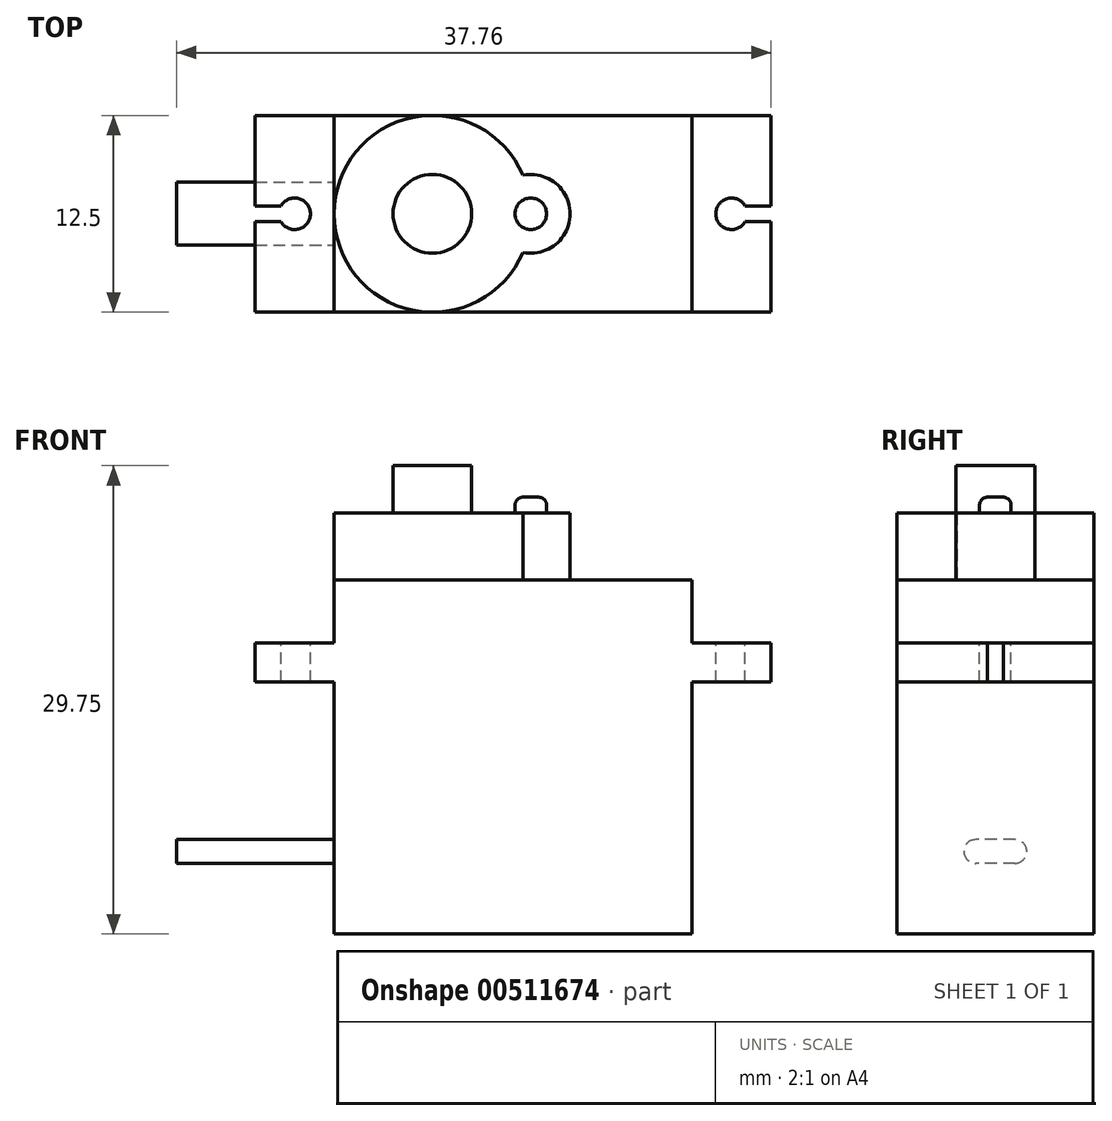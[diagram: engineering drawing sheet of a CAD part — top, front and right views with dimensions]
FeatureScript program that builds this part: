
annotation { "Feature Type Name" : "Feature", "Feature Type Description" : "" }
export const myFeature = defineFeature(function(context is Context, id is Id, definition is map)
    precondition{}
    {
        {
            var Q0;
            Q0=qCreatedBy(makeId("Top.planeOp"),FACE);
            var sketch = newSketch(context, id + "F0", { "sketchPlane" : qUnion([Q0])});
            skLineSegment(sketch, "E0.bottom", {"start": v(11.38, 6.25) * mm, "end": v(-11.37, 6.25) * mm});
            skLineSegment(sketch, "E0.top", {"start": v(11.37, -6.25) * mm, "end": v(-11.38, -6.25) * mm});
            skLineSegment(sketch, "E0.left", {"start": v(11.38, 6.25) * mm, "end": v(11.37, -6.25) * mm});
            skLineSegment(sketch, "E0.right", {"start": v(-11.37, 6.25) * mm, "end": v(-11.38, -6.25) * mm});
            skPoint(sketch, "E0.middle", {"position": v(0, 0) * mm});
            skSolve(sketch);
        }
        {
            var Q0;
            Q0=makeQuery(id+"F0.imprint","IMPRINT",FACE,{"disambiguationData":[TD([[makeQuery(id+"F0.imprint","IMPRINT",EDGE,{"derivedFrom":sQuery(id+"F0.wireOp",EDGE,"E0.bottom")}),1.0]])]});
            extrude(context, id + "F1", {"entities" : qUnion([Q0]), "depth" : 22.5 * mm});
        }
        {
            var Q0;
            Q0=qCreatedBy(makeId("Top.planeOp"),FACE);
            cPlane(context, id + "F2", {"entities" : qUnion([Q0]), "cplaneType" : CPlaneType.OFFSET, "offset" : 16 * mm, "width" : 150 * mm, "height" : 150 * mm});
        }
        {
            var Q0;
            Q0=qCreatedBy(id+"F2.planeOp",FACE);
            var sketch = newSketch(context, id + "F3", { "sketchPlane" : qUnion([Q0])});
            skLineSegment(sketch, "E1.bottom", {"start": v(11.38, 6.25) * mm, "end": v(16.38, 6.25) * mm});
            skLineSegment(sketch, "E1.top", {"start": v(11.38, -6.25) * mm, "end": v(16.38, -6.25) * mm});
            skLineSegment(sketch, "E1.left", {"start": v(11.38, 6.25) * mm, "end": v(11.38, -6.25) * mm});
            skLineSegment(sketch, "E1.right", {"start": v(16.38, 6.25) * mm, "end": v(16.38, -6.25) * mm});
            skLineSegment(sketch, "E2.bottom", {"start": v(-16.38, 6.25) * mm, "end": v(-11.37, 6.25) * mm});
            skLineSegment(sketch, "E2.top", {"start": v(-16.38, -6.25) * mm, "end": v(-11.38, -6.25) * mm});
            skLineSegment(sketch, "E2.left", {"start": v(-16.38, 6.25) * mm, "end": v(-16.38, -6.25) * mm});
            skLineSegment(sketch, "E2.right", {"start": v(-11.37, 6.25) * mm, "end": v(-11.37, -6.25) * mm});
            skSolve(sketch);
        }
        {
            var Q0;
            Q0=makeQuery(id+"F3.imprint","IMPRINT",FACE,{"disambiguationData":[TD([[makeQuery(id+"F3.imprint","IMPRINT",EDGE,{"derivedFrom":sQuery(id+"F3.wireOp",EDGE,"E2.bottom")}),-1.0]])]});
            var Q1;
            Q1=makeQuery(id+"F3.imprint","IMPRINT",FACE,{"disambiguationData":[TD([[makeQuery(id+"F3.imprint","IMPRINT",EDGE,{"derivedFrom":sQuery(id+"F3.wireOp",EDGE,"E1.bottom")}),-1.0]])]});
            extrude(context, id + "F4", {"entities" : qUnion([Q0, Q1]), "operationType" : NewBodyOperationType.ADD, "depth" : 2.5 * mm});
        }
        {
            var Q0;
            Q0=makeQuery(id+"F4.opExtrude","CAP_FACE",FACE,{"disambiguationData":[OSD([sQuery(id+"F3.wireOp",EDGE,"E2.bottom"),sQuery(id+"F3.wireOp",EDGE,"E2.top"),sQuery(id+"F3.wireOp",EDGE,"E2.left"),sQuery(id+"F3.wireOp",EDGE,"E2.right")])],"isStart":false});
            var sketch = newSketch(context, id + "F5", { "sketchPlane" : qUnion([Q0])});
            skArc(sketch, "E3", {"start": v(-14.74, -0.5) * mm, "mid": v(-12.88, 0) * mm, "end": v(-14.74, 0.5) * mm});
            skArc(sketch, "E4", {"start": v(14.74, 0.5) * mm, "mid": v(12.88, 0) * mm, "end": v(14.74, -0.5) * mm});
            skLineSegment(sketch, "E5", {"start": v(-13.88, 0) * mm, "end": v(-16.38, 0) * mm, "construction": true});
            skLineSegment(sketch, "E6", {"start": v(13.88, 0) * mm, "end": v(16.38, 0) * mm, "construction": true});
            skLineSegment(sketch, "E7.0", {"start": v(-14.74, 0.5) * mm, "end": v(-16.38, 0.5) * mm});
            skLineSegment(sketch, "E8.0", {"start": v(-14.74, -0.5) * mm, "end": v(-16.38, -0.5) * mm});
            skLineSegment(sketch, "E9", {"start": v(-16.38, 0.5) * mm, "end": v(-16.38, -0.5) * mm});
            skLineSegment(sketch, "E10.0", {"start": v(14.74, -0.5) * mm, "end": v(16.38, -0.5) * mm});
            skLineSegment(sketch, "E11.0", {"start": v(14.74, 0.5) * mm, "end": v(16.38, 0.5) * mm});
            skLineSegment(sketch, "E12", {"start": v(16.38, 0.5) * mm, "end": v(16.38, -0.5) * mm});
            skSolve(sketch);
        }
        {
            var Q0;
            Q0=makeQuery(id+"F5.imprint","IMPRINT",FACE,{"disambiguationData":[TD([[makeQuery(id+"F5.imprint","IMPRINT",EDGE,{"derivedFrom":sQuery(id+"F5.wireOp",EDGE,"E3")}),1.0]])]});
            var Q1;
            Q1=makeQuery(id+"F5.imprint","IMPRINT",FACE,{"disambiguationData":[TD([[makeQuery(id+"F5.imprint","IMPRINT",EDGE,{"derivedFrom":sQuery(id+"F5.wireOp",EDGE,"E4")}),1.0]])]});
            extrude(context, id + "F6", {"entities" : qUnion([Q0, Q1]), "operationType" : NewBodyOperationType.REMOVE, "endBound" : BoundingType.UP_TO_NEXT, "oppositeDirection" : true, "depth" : 25 * mm});
        }
        {
            var Q0;
            Q0=makeQuery(id+"F1.opExtrude","CAP_FACE",FACE,{"disambiguationData":[OSD([sQuery(id+"F0.wireOp",EDGE,"E0.bottom"),sQuery(id+"F0.wireOp",EDGE,"E0.top"),sQuery(id+"F0.wireOp",EDGE,"E0.left"),sQuery(id+"F0.wireOp",EDGE,"E0.right")])],"isStart":false});
            var sketch = newSketch(context, id + "F7", { "sketchPlane" : qUnion([Q0])});
            skArc(sketch, "E13", {"start": v(0.63, 2.45) * mm, "mid": v(-11.37, 0) * mm, "end": v(0.63, -2.45) * mm});
            skArc(sketch, "E14", {"start": v(0.63, -2.45) * mm, "mid": v(3.63, 0) * mm, "end": v(0.63, 2.45) * mm});
            skSolve(sketch);
        }
        {
            var Q0;
            {var subQ0=sQuery(id+"F7.wireOp",EDGE,"E14");Q0=makeQuery(id+"F7.imprint","IMPRINT",FACE,{"disambiguationData":[TD([[makeQuery(id+"F7.imprint","IMPRINT",EDGE,{"derivedFrom":subQ0}),1.0]])]});}
            extrude(context, id + "F8", {"entities" : qUnion([Q0]), "operationType" : NewBodyOperationType.ADD, "depth" : 4.25 * mm});
        }
        {
            var Q0;
            Q0=makeQuery(id+"F8.opExtrude","CAP_FACE",FACE,{"disambiguationData":[OSD([sQuery(id+"F7.wireOp",EDGE,"E13"),sQuery(id+"F7.wireOp",EDGE,"E14")])],"isStart":false});
            var sketch = newSketch(context, id + "F9", { "sketchPlane" : qUnion([Q0])});
            skCircle(sketch, "E15", {"center": v(1.13, 0) * mm, "radius": 1 * mm});
            skSolve(sketch);
        }
        {
            var Q0;
            Q0=makeQuery(id+"F9.imprint","IMPRINT",FACE,{"disambiguationData":[TD([[makeQuery(id+"F9.imprint","IMPRINT",EDGE,{"derivedFrom":sQuery(id+"F9.wireOp",EDGE,"E15")}),1.0]])]});
            extrude(context, id + "F10", {"entities" : qUnion([Q0]), "operationType" : NewBodyOperationType.ADD, "depth" : 1 * mm});
        }
        {
            var Q0;
            Q0=makeQuery(id+"F8.opExtrude","CAP_FACE",FACE,{"disambiguationData":[OSD([sQuery(id+"F7.wireOp",EDGE,"E13"),sQuery(id+"F7.wireOp",EDGE,"E14")])],"isStart":false});
            var sketch = newSketch(context, id + "F11", { "sketchPlane" : qUnion([Q0])});
            skCircle(sketch, "E16", {"center": v(-5.12, 0) * mm, "radius": 2.5 * mm});
            skSolve(sketch);
        }
        {
            var Q0;
            Q0=makeQuery(id+"F11.imprint","IMPRINT",FACE,{"disambiguationData":[TD([[makeQuery(id+"F11.imprint","IMPRINT",EDGE,{"derivedFrom":sQuery(id+"F11.wireOp",EDGE,"E16")}),1.0]])]});
            extrude(context, id + "F12", {"entities" : qUnion([Q0]), "operationType" : NewBodyOperationType.ADD, "depth" : 3 * mm});
        }
        {
            var Q0;
            {var subQ0=sQuery(id+"F0.wireOp",EDGE,"E0.top");var subQ2=sQuery(id+"F0.wireOp",EDGE,"E0.right");var subQ3=sQuery(id+"F0.wireOp",EDGE,"E0.bottom");Q0=makeQuery(id+"F4.boolean.opBoolean","SPLIT",FACE,{"disambiguationData":[TD([makeQuery(id+"F1.opExtrude","CAP_FACE",FACE,{"disambiguationData":[OSD([subQ3,subQ0,sQuery(id+"F0.wireOp",EDGE,"E0.left"),subQ2])],"isStart":true})])],"derivedFrom":makeQuery(id+"F1.opExtrude","SWEPT_FACE",FACE,{"disambiguationData":[OSD([subQ2])]})});}
            var sketch = newSketch(context, id + "F13", { "sketchPlane" : qUnion([Q0])});
            skLineSegment(sketch, "E17.bottom", {"start": v(-1.25, 6) * mm, "end": v(1.25, 6) * mm});
            skLineSegment(sketch, "E17.top", {"start": v(-1.25, 4.5) * mm, "end": v(1.25, 4.5) * mm});
            skLineSegment(sketch, "E17.left", {"start": v(-2, 5.25) * mm, "end": v(-2, 5.25) * mm});
            skLineSegment(sketch, "E17.right", {"start": v(2, 5.25) * mm, "end": v(2, 5.25) * mm});
            skPoint(sketch, "E18.visualSharp", {"position": v(-2, 6) * mm});
            skArc(sketch, "E18.filletArc", {"start": v(-1.25, 6) * mm, "mid": v(-1.78, 5.78) * mm, "end": v(-2, 5.25) * mm});
            skPoint(sketch, "E19.visualSharp", {"position": v(-2, 4.5) * mm});
            skArc(sketch, "E19.filletArc", {"start": v(-2, 5.25) * mm, "mid": v(-1.78, 4.72) * mm, "end": v(-1.25, 4.5) * mm});
            skPoint(sketch, "E20.visualSharp", {"position": v(2, 6) * mm});
            skArc(sketch, "E20.filletArc", {"start": v(2, 5.25) * mm, "mid": v(1.78, 5.78) * mm, "end": v(1.25, 6) * mm});
            skPoint(sketch, "E21.visualSharp", {"position": v(2, 4.5) * mm});
            skArc(sketch, "E21.filletArc", {"start": v(1.25, 4.5) * mm, "mid": v(1.78, 4.72) * mm, "end": v(2, 5.25) * mm});
            skSolve(sketch);
        }
        {
            var Q0;
            Q0=makeQuery(id+"F13.imprint","IMPRINT",FACE,{"disambiguationData":[TD([[makeQuery(id+"F13.imprint","IMPRINT",EDGE,{"derivedFrom":sQuery(id+"F13.wireOp",EDGE,"E17.bottom")}),-1.0]])]});
            extrude(context, id + "F14", {"entities" : qUnion([Q0]), "operationType" : NewBodyOperationType.ADD, "depth" : 10 * mm});
        }
        {
            var Q0;
            Q0=makeQuery(id+"F10.opExtrude","CAP_EDGE",EDGE,{"disambiguationData":[OSD([sQuery(id+"F9.wireOp",EDGE,"E15")])],"isStart":false});
            fillet(context, id + "F15", {"entities" : qUnion([Q0]), "radius" : 0.5 * mm, "tangentPropagation" : true, "allowEdgeOverflow" : false});
        }
    });
